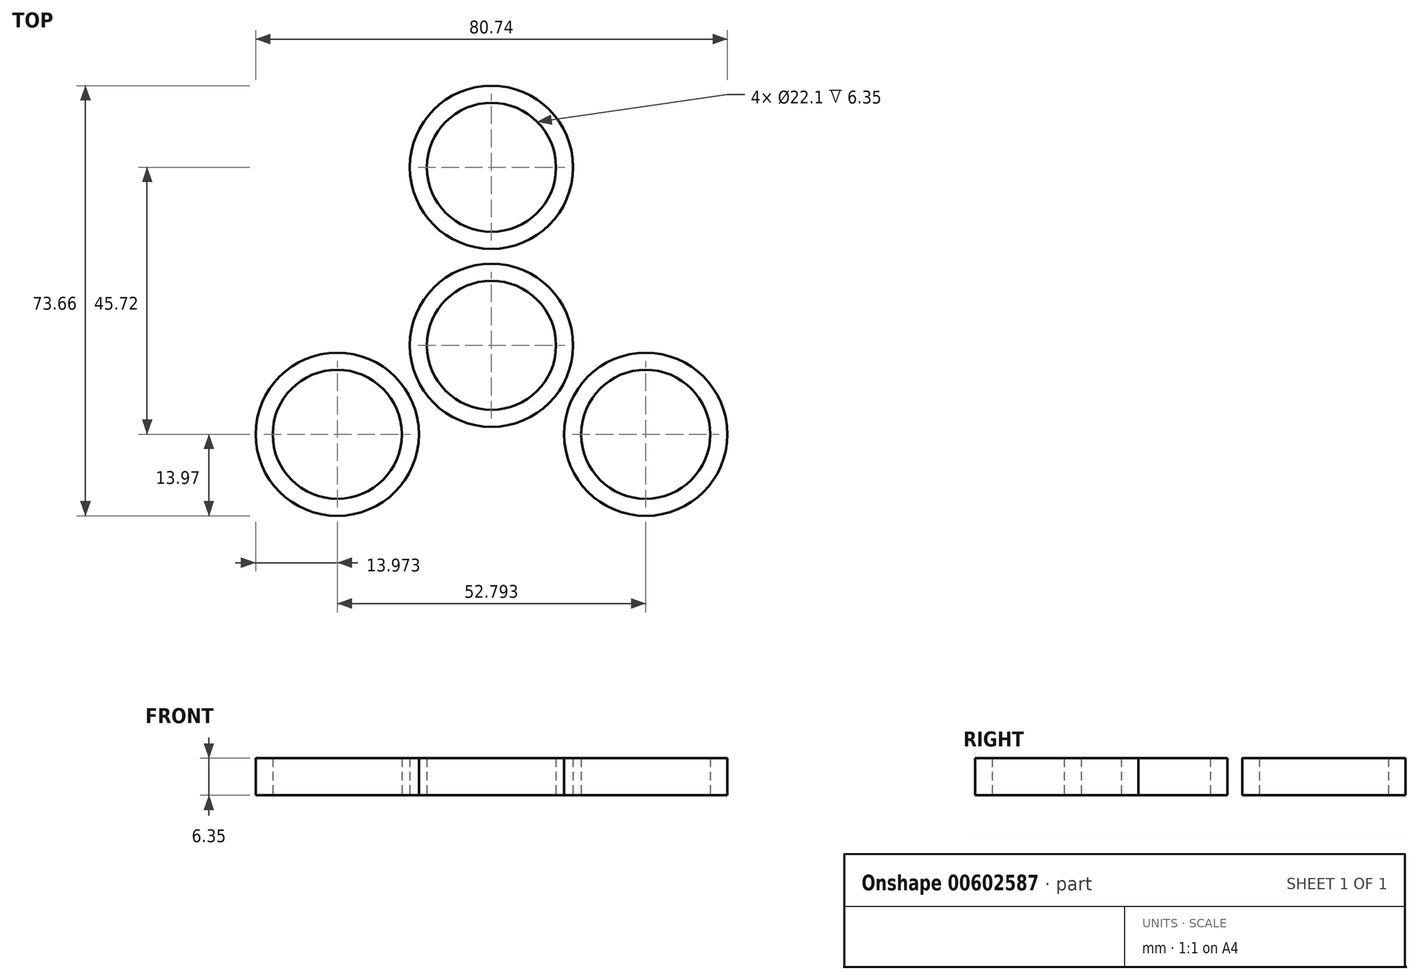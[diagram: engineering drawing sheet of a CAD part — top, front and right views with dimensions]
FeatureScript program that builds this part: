
annotation { "Feature Type Name" : "Feature", "Feature Type Description" : "" }
export const myFeature = defineFeature(function(context is Context, id is Id, definition is map)
    precondition{}
    {
        {
            var Q0;
            Q0=qCreatedBy(makeId("Top.planeOp"),FACE);
            var sketch = newSketch(context, id + "F0", { "sketchPlane" : qUnion([Q0])});
            skCircle(sketch, "E0", {"center": v(0, 0) * mm, "radius": 11.05 * mm});
            skCircle(sketch, "E1", {"center": v(0, 0) * mm, "radius": 13.97 * mm});
            skLineSegment(sketch, "E2", {"start": v(0, 0) * mm, "end": v(0, 30.48) * mm});
            skCircle(sketch, "E3", {"center": v(0, 30.48) * mm, "radius": 11.05 * mm});
            skCircle(sketch, "E4", {"center": v(0, 30.48) * mm, "radius": 13.97 * mm});
            skCircle(sketch, "E5.1.0", {"center": v(-26.4, -15.24) * mm, "radius": 11.05 * mm});
            skCircle(sketch, "E5.1.1", {"center": v(-26.4, -15.24) * mm, "radius": 13.97 * mm});
            skCircle(sketch, "E5.2.0", {"center": v(26.4, -15.24) * mm, "radius": 11.05 * mm});
            skCircle(sketch, "E5.2.1", {"center": v(26.4, -15.24) * mm, "radius": 13.97 * mm});
            skSolve(sketch);
        }
        {
            var Q0;
            Q0=qCreatedBy(makeId("Top.planeOp"),FACE);
            var sketch = newSketch(context, id + "F1", { "sketchPlane" : qUnion([Q0])});
            skFitSpline(sketch, "E6", {"points": [v(-12.75, 25.2) * mm, v(-11.2, 8.86) * mm, v(-27.74, -1.46) * mm], "startDerivative": vector(11.63, -37.61) * mm, "endDerivative": vector(-40.86, -16.04) * mm});
            skFitSpline(sketch, "E7", {"points": [v(-14.9, -23.46) * mm, v(0, -14.11) * mm, v(16.45, -25.2) * mm], "startDerivative": vector(30.42, 29.17) * mm, "endDerivative": vector(32.25, -32.05) * mm});
            skFitSpline(sketch, "E8", {"points": [v(13.14, 25.6) * mm, v(10.91, 8.86) * mm, v(26.38, -1.65) * mm], "startDerivative": vector(-13.03, -37.73) * mm, "endDerivative": vector(39.07, -16.95) * mm});
            skSolve(sketch);
        }
        {
            var Q0;
            Q0=makeQuery(id+"F0.imprint","IMPRINT",FACE,{"disambiguationData":[TD([[makeQuery(id+"F0.imprint","IMPRINT",EDGE,{"derivedFrom":sQuery(id+"F0.wireOp",EDGE,"E3")}),-1.0]])]});
            var Q1;
            Q1=makeQuery(id+"F0.imprint","IMPRINT",FACE,{"disambiguationData":[TD([[makeQuery(id+"F0.imprint","IMPRINT",EDGE,{"derivedFrom":sQuery(id+"F0.wireOp",EDGE,"E5.1.0")}),-1.0]])]});
            var Q2;
            Q2=makeQuery(id+"F0.imprint","IMPRINT",FACE,{"disambiguationData":[TD([[makeQuery(id+"F0.imprint","IMPRINT",EDGE,{"derivedFrom":sQuery(id+"F0.wireOp",EDGE,"E5.2.0")}),-1.0]])]});
            var Q3;
            Q3=makeQuery(id+"F0.imprint","IMPRINT",FACE,{"disambiguationData":[TD([[makeQuery(id+"F0.imprint","IMPRINT",EDGE,{"derivedFrom":sQuery(id+"F0.wireOp",EDGE,"E0")}),-1.0]])]});
            extrude(context, id + "F2", {"entities" : qUnion([Q0, Q1, Q2, Q3]), "depth" : 6.35 * mm, "offsetDistance" : 25.4 * mm});
        }
        {
            var Q0;
            Q0=sQuery(id+"F1.wireOp",EDGE,"E6");
            var Q1;
            Q1=sQuery(id+"F1.wireOp",EDGE,"E8");
            var Q2;
            Q2=sQuery(id+"F1.wireOp",EDGE,"E7");
            extrude(context, id + "F3", {"bodyType" : ToolBodyType.SURFACE, "surfaceEntities" : qUnion([Q0, Q1, Q2]), "depth" : 6.35 * mm, "offsetDistance" : 25.4 * mm});
        }
    });
